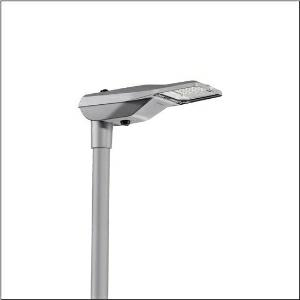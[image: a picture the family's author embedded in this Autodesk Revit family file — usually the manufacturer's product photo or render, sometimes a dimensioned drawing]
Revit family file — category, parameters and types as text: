
# Revit family: streetlight_sl_21_micro___st1_5a_5xe1p43t08db_e62a
name_source: partatom
category: Lighting Fixtures
units: mm (PartAtom-declared; Revit-internal decimal feet)

## family parameters
Cut with Voids When Loaded = No
Host = Face
Light Source = No
Part Type = Normal
Room Calculation Point = No
Round Connector Dimension = Use Diameter
Shared = No

## types (1)
- --- (1 x LED, 5230 lm, 39.1 W, 4000K)
    Apparent Load = 39 VA
    CIE Flux Codes = 22 53 95 100 100
    Color Rendering = 70
    Color Temperature = 4000K
    Default Elevation = 1800 mm
    Description = Streetlight SL 21 micro, mast luminaire, primary light control with lens, of PMMA, primary optical cover: cover, of toughened safety glass, transparent, light distribution: ST1.5a, light emission: direct distribution, primary light characteristic: asymmetric, installation type: side-entry, post-top, LED, High Power LED, rated luminous flux: 5.230lm, luminous efficacy: 134lm/W, light colour: 740, colour temperature: 4000K, control gear: D4i, control: flexible luminous flux parameterisation, time-dependent luminous flux control, constant luminous flux control, overheat protection, pre-setting: logarithmic dimming characteristic, mains connection: 220..240V, AC, 50/60Hz, start of lifetime: 39W, end of service life: 41W, reduction: 18W, luminaire housing, of diecast aluminium, powder-coated, Siteco® metallic grey (DB 702S), corrosivity category C5 mid according to DIN EN ISO 12944, please order mast flange separately, inclination adjustable: 0°, 5°, 10°, 15°, sealing non-destructively replaceable, multi-level sealing system, length: 528mm, width: 235mm, height: 110mm, mast flange for spigot size: 42mm (side-entry): 5XC10008XM4, 60/48mm (side-entry/post-top): 5XC10108XM2, 76/60mm (side-entry/post-top): 5XC10108XM1, Smart Interface below and above, protection rating (complete): IP66, insulation class (complete): insulation class II (safety insulation), certification: CE, ENEC, ENEC+, VDE, impact resistance: IK10, permissible operating ambient temperature for outdoor applications: -40..+50°C, standard-compliant lighting for roads and squares, packaging unit: 1 piece

Light Distribution: ST1.5a
    Height = 110 mm
    Lamp = 1 x LED
    Lamp Light Flux = 5230 lm
    Lamp Power = 39.1 W
    Lamp count = 1
    Length = 528 mm
    Luminous efficacy = 134 lm/W
    Manufacturer = Siteco
    ModVariant = No
    Model = 5XE1P43T08DB
    Number of Poles = 1
    OnlyDefault = Yes
    Power Factor = 1
    Product Name = Streetlight SL 21 micro | ST1.5a
    Product group = mast luminaire | pylon top
    ProductGroupID = 6100
    Protection Class = Protection class II
    Protection Degree = IP 66
    RLX_Detail_Level = 1
    RLX_Emergency_Light_Flux = 0 lm
    RLX_Emergency_Type = 0
    RLX_Emergency_Type_DB = No
    RlxData = <blob elided: 101697 chars, md5=a7e29f7f>
    Socket = socket
    Standby Power = 0 W
    System Light Flux = 5230 lm
    System Power = 39 W
    Type Comments = factory setting: luminous flux: 100 % | dim-lin: 254 | 765 mA
    Type Image = l_1007239.jpg
    URL = http://relux.com
    VarID = @adj_153674
    Voltage = 0 V
    Weight = 0.00 kg
    Width = 235 mm

## geometry (parser evidence)
native form markers: Blend x4, Sweep x9
no freeform markers — native parametric forms only
